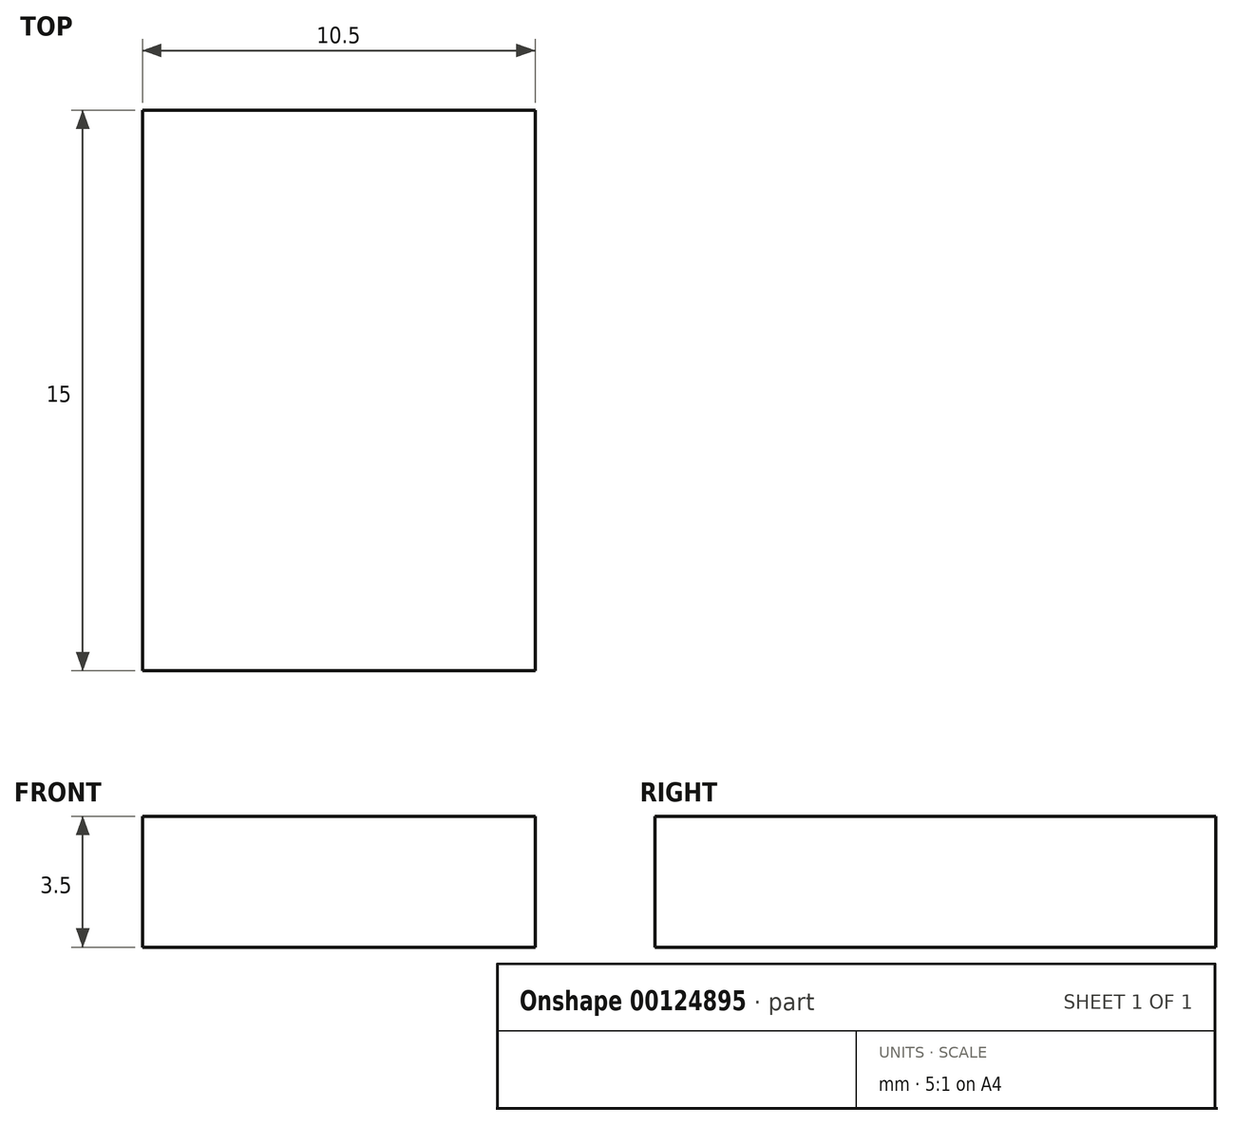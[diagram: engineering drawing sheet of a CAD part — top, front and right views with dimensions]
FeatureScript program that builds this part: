
annotation { "Feature Type Name" : "Feature", "Feature Type Description" : "" }
export const myFeature = defineFeature(function(context is Context, id is Id, definition is map)
    precondition{}
    {
        {
            var Q0;
            Q0=qCreatedBy(makeId("Top.planeOp"),FACE);
            var sketch = newSketch(context, id + "F0", { "sketchPlane" : qUnion([Q0])});
            skLineSegment(sketch, "E0", {"start": v(0, 0) * mm, "end": v(10.5, 0) * mm});
            skLineSegment(sketch, "E1", {"start": v(10.5, 0) * mm, "end": v(10.5, 15) * mm});
            skLineSegment(sketch, "E2", {"start": v(10.5, 15) * mm, "end": v(0, 15) * mm});
            skLineSegment(sketch, "E3", {"start": v(0, 15) * mm, "end": v(0, 0) * mm});
            skSolve(sketch);
        }
        {
            var Q0;
            Q0=makeQuery(id+"F0.imprint","IMPRINT",FACE,{"disambiguationData":[TD([[makeQuery(id+"F0.imprint","IMPRINT",EDGE,{"derivedFrom":sQuery(id+"F0.wireOp",EDGE,"E0")}),1.0]])]});
            extrude(context, id + "F1", {"entities" : qUnion([Q0]), "depth" : 3.5 * mm});
        }
    });
